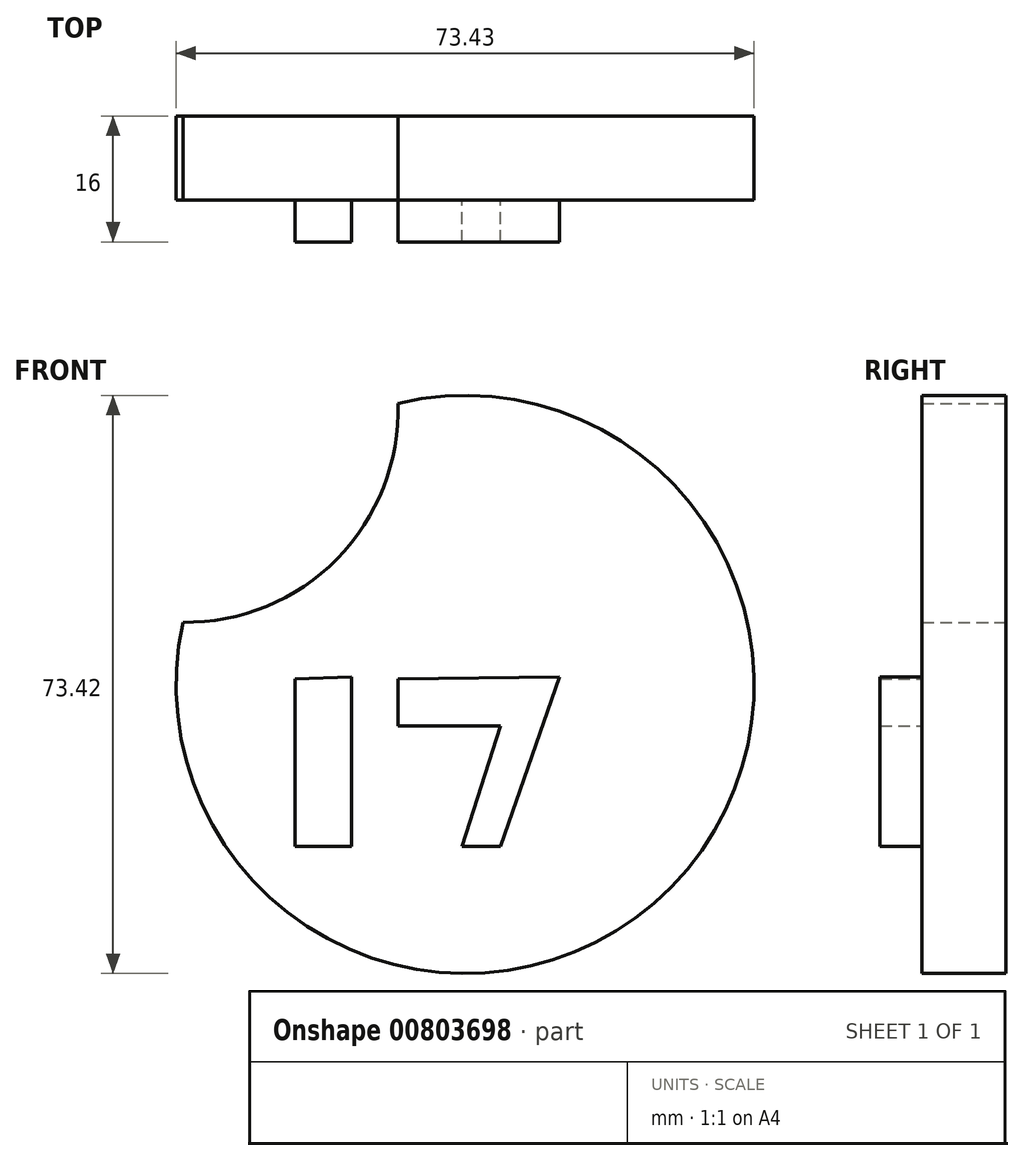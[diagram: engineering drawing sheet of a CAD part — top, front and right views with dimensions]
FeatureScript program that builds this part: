
annotation { "Feature Type Name" : "Feature", "Feature Type Description" : "" }
export const myFeature = defineFeature(function(context is Context, id is Id, definition is map)
    precondition{}
    {
        {
            var Q0;
            Q0=qCreatedBy(makeId("Front.planeOp"),FACE);
            var sketch = newSketch(context, id + "F0", { "sketchPlane" : qUnion([Q0])});
            skArc(sketch, "E0", {"start": v(0, -27.82) * mm, "mid": v(62.04, -61.43) * mm, "end": v(27.32, 0) * mm});
            skArc(sketch, "E1", {"start": v(0, -27.82) * mm, "mid": v(19.6, -19.74) * mm, "end": v(27.32, 0) * mm});
            skSolve(sketch);
        }
        {
            var Q0;
            Q0=makeQuery(id+"F0.imprint","IMPRINT",FACE,{"disambiguationData":[TD([[makeQuery(id+"F0.imprint","IMPRINT",EDGE,{"derivedFrom":sQuery(id+"F0.wireOp",EDGE,"E0")}),1.0]])]});
            extrude(context, id + "F1", {"entities" : qUnion([Q0]), "depth" : 5.33 * mm, "offsetDistance" : 25.4 * mm});
        }
        {
            var Q0;
            Q0=makeQuery(id+"F1.opExtrude","CAP_FACE",FACE,{"disambiguationData":[OSD([sQuery(id+"F0.wireOp",EDGE,"E0"),sQuery(id+"F0.wireOp",EDGE,"E1")])],"isStart":false});
            extrude(context, id + "F2", {"entities" : qUnion([Q0]), "operationType" : NewBodyOperationType.ADD, "depth" : 5.33 * mm, "offsetDistance" : 25.4 * mm});
        }
        {
            var Q0;
            Q0=makeQuery(id+"F2.opExtrude","CAP_FACE",FACE,{"disambiguationData":[OSD([sQuery(id+"F0.wireOp",EDGE,"E0"),sQuery(id+"F0.wireOp",EDGE,"E1")])],"isStart":false});
            var sketch = newSketch(context, id + "F3", { "sketchPlane" : qUnion([Q0])});
            skLineSegment(sketch, "E2", {"start": v(14.24, -35.03) * mm, "end": v(14.24, -56.27) * mm});
            skLineSegment(sketch, "E3", {"start": v(14.24, -56.27) * mm, "end": v(21.41, -56.27) * mm});
            skLineSegment(sketch, "E4", {"start": v(21.41, -56.27) * mm, "end": v(21.41, -34.75) * mm});
            skLineSegment(sketch, "E5", {"start": v(21.41, -34.75) * mm, "end": v(14.24, -35.03) * mm});
            skLineSegment(sketch, "E6", {"start": v(27.32, -35.03) * mm, "end": v(47.82, -34.75) * mm});
            skLineSegment(sketch, "E7", {"start": v(47.82, -34.75) * mm, "end": v(40.32, -56.27) * mm});
            skLineSegment(sketch, "E8", {"start": v(40.32, -56.27) * mm, "end": v(35.43, -56.27) * mm});
            skLineSegment(sketch, "E9", {"start": v(35.43, -56.27) * mm, "end": v(40.32, -40.95) * mm});
            skLineSegment(sketch, "E10", {"start": v(40.32, -40.95) * mm, "end": v(27.32, -40.95) * mm});
            skLineSegment(sketch, "E11", {"start": v(27.32, -40.95) * mm, "end": v(27.32, -35.03) * mm});
            skSolve(sketch);
        }
        {
            var Q0;
            Q0=makeQuery(id+"F3.imprint","IMPRINT",FACE,{"disambiguationData":[TD([[makeQuery(id+"F3.imprint","IMPRINT",EDGE,{"derivedFrom":sQuery(id+"F3.wireOp",EDGE,"E6")}),-1.0]])]});
            var Q1;
            Q1=makeQuery(id+"F3.imprint","IMPRINT",FACE,{"disambiguationData":[TD([[makeQuery(id+"F3.imprint","IMPRINT",EDGE,{"derivedFrom":sQuery(id+"F3.wireOp",EDGE,"E2")}),1.0]])]});
            extrude(context, id + "F4", {"entities" : qUnion([Q0, Q1]), "operationType" : NewBodyOperationType.ADD, "depth" : 5.33 * mm, "offsetDistance" : 25.4 * mm});
        }
    });
